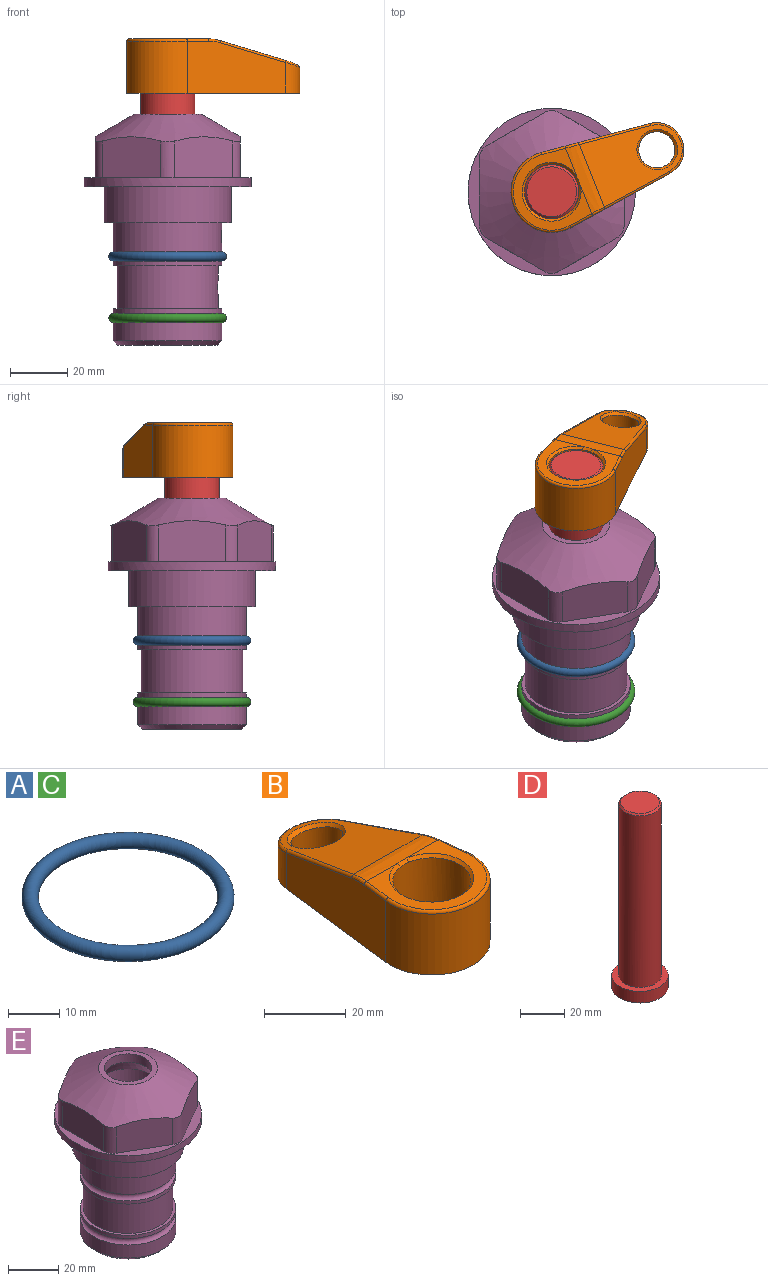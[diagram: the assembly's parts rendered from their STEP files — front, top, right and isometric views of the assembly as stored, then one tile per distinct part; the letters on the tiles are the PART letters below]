
ASSEMBLY  parts=5 mates=4
PART A: 1 faces, bbox 44.7x44.7x3.2 mm
  f0: torus R=19.05mm, axis (0,0,1), area 1193.9mm2
PART B: 31 faces, bbox 31.7x65.5x19.8 mm
  f0: plane 39.12x18.26mm, normal (0.99,0.12,0), area 612.2mm2, adj f1,f4,f7,f11,f13,f15
  f1: cylinder r=9.53mm len=18.91mm, axis (0,0,-1), area 296.1mm2, adj f0,f2,f7,f17
  f2: plane 39.12x18.26mm, normal (-0.99,0.12,0), area 612.2mm2, adj f1,f4,f7,f12,f14,f16
  f3: cylinder r=6.35mm len=12.7mm, axis (0,0,-1), area 362.4mm2, adj f7,f18
  f4: cylinder r=14.29mm len=28.58mm, axis (0,0,-1), area 882.2mm2, adj f0,f2,f7,f10
  f5: cylinder r=9.53mm len=19.05mm, axis (0,0,-1), area 1092.6mm2, adj f7,f19,f20
  f6: plane 26.99x23.69mm, normal (0,0,1), area 216.2mm2, adj f9,f10,f11,f12,f19
  f7: plane 63.5x28.58mm, normal (0,0,-1), area 661.8mm2, adj f0,f1,f2,f3,f4,f5,f22,f23
  f8: plane 33.52x23.6mm, normal (0,0.26,0.97), area 486mm2, adj f9,f15,f16,f17,f18
  f9: cylinder r=19.05mm len=24.72mm, axis (1,0,0), area 120.4mm2, adj f6,f8,f13,f14,f20
  f10: torus R=13.49mm, axis (0,0,1), area 59mm2, adj f4,f6,f11,f12
  f11: cylinder r=0.79mm len=8.67mm, axis (0.12,-0.99,0), area 10.8mm2, adj f0,f6,f10,f13
  f12: cylinder r=0.79mm len=8.67mm, axis (0.12,0.99,0), area 10.8mm2, adj f2,f6,f10,f14
  f13: bspline ~4.95x1.42mm, area 6.1mm2, adj f0,f9,f11,f15
  f14: bspline ~4.95x1.42mm, area 6.1mm2, adj f2,f9,f12,f16
  f15: cylinder r=0.79mm len=25.95mm, axis (0.12,-0.96,0.26), area 32.9mm2, adj f0,f8,f13,f17
  f16: cylinder r=0.79mm len=25.95mm, axis (0.12,0.96,-0.26), area 32.9mm2, adj f2,f8,f14,f17
  f17: bspline ~18.91x8.38mm, area 30mm2, adj f1,f8,f15,f16
  f18: bspline ~14.29x14.29mm, area 48.3mm2, adj f3,f8
  f19: cone r=9.53mm half-angle=45deg, axis (0,0,1), area 66.5mm2, adj f5,f6,f20
  f20: bspline ~3.22x0.96mm, area 3.5mm2, adj f5,f9,f19
  f21: plane 2.75x2.72mm, normal (0,0,-1), area 2.9mm2, adj f23,f25,f28
  f22: plane 23.05x15.88mm, normal (-0.99,-0.12,0), area 323.6mm2, adj f7,f25,f26,f27,f28,f29
  f23: plane 23.05x15.88mm, normal (0.99,-0.12,0), area 323.6mm2, adj f7,f21,f25,f27,f28,f30
  f24: cylinder r=9.53mm len=10.69mm, axis (0,0,-1), area 114.7mm2, adj f7,f27,f29,f30
  f25: cylinder r=12.7mm len=20.59mm, axis (0,0,-1), area 381.1mm2, adj f7,f21,f22,f23,f26,f28
  f26: plane 2.75x2.72mm, normal (0,0,-1), area 2.9mm2, adj f22,f25,f28
  f27: plane 19.72x18.37mm, normal (0,-0.26,-0.97), area 291.8mm2, adj f22,f23,f24,f28,f29,f30
  f28: cylinder r=15.88mm len=19.92mm, axis (1,0,0), area 54.8mm2, adj f21,f22,f23,f25,f26,f27
  f29: cylinder r=1.59mm len=11mm, axis (0,0,-1), area 34.7mm2, adj f7,f22,f24,f27
  f30: cylinder r=1.59mm len=11mm, axis (0,0,-1), area 34.7mm2, adj f7,f23,f24,f27
PART C: same geometry as A
PART D: 6 faces, bbox 25.4x25.4x101.6 mm
  f0: plane 17.46x17.46mm, normal (0,0,1), area 239.5mm2, adj f5
  f1: plane 25.4x25.4mm, normal (0,0,-1), area 506.7mm2, adj f2
  f2: cylinder r=12.7mm len=25.4mm, axis (0,0,1), area 506.7mm2, adj f1,f3
  f3: plane 25.4x25.4mm, normal (0,0,1), area 221.7mm2, adj f2,f4
  f4: cylinder r=9.53mm len=94.46mm, axis (0,0,1), area 5653mm2, adj f3,f5
  f5: cone r=8.73mm half-angle=45deg, axis (0,0,-1), area 64.4mm2, adj f0,f4
PART E: 36 faces, bbox 58.7x58.7x81 mm
  f0: cylinder r=17.78mm len=35.56mm, axis (0,0,1), area 1670.8mm2, adj f23,f24,f31
  f1: cylinder r=19.05mm len=38.1mm, axis (0,0,1), area 1191.9mm2, adj f26,f27,f30
  f2: plane 58.66x58.66mm, normal (0,0,-1), area 1150.6mm2, adj f3,f28
  f3: cylinder r=29.33mm len=58.66mm, axis (0,0,-1), area 585.1mm2, adj f2,f4
  f4: plane 58.66x58.66mm, normal (0,0,1), area 475.9mm2, adj f3,f5,f6,f7,f8,f9,f10,f11
  f5: plane 20.32x14.34mm, normal (-0.5,0.87,0), area 324.4mm2, adj f4,f15,f16,f17
  f6: plane 20.32x14.34mm, normal (0.5,0.87,0), area 324.4mm2, adj f4,f14,f15,f17
  f7: plane 23.48x14.34mm, normal (1,0,0), area 324.4mm2, adj f4,f13,f14,f17
  f8: plane 20.32x14.34mm, normal (0.5,-0.87,0), area 324.4mm2, adj f4,f12,f13,f17
  f9: plane 20.32x14.34mm, normal (-0.5,-0.87,0), area 324.4mm2, adj f4,f11,f12,f17
  f10: plane 23.48x14.34mm, normal (-1,0,0), area 324.4mm2, adj f4,f11,f16,f17
  f11: cylinder r=5.08mm len=12.85mm, axis (0,0,-1), area 67.2mm2, adj f4,f9,f10,f17
  f12: cylinder r=5.08mm len=12.85mm, axis (0,0,-1), area 67.2mm2, adj f4,f8,f9,f17
  f13: cylinder r=5.08mm len=12.85mm, axis (0,0,-1), area 67.2mm2, adj f4,f7,f8,f17
  f14: cylinder r=5.08mm len=12.85mm, axis (0,0,-1), area 67.2mm2, adj f4,f6,f7,f17
  f15: cylinder r=5.08mm len=12.85mm, axis (0,0,-1), area 67.2mm2, adj f4,f5,f6,f17
  f16: cylinder r=5.08mm len=12.85mm, axis (0,0,-1), area 67.2mm2, adj f4,f5,f10,f17
  f17: cone r=11.73mm half-angle=60deg, axis (0,0,-1), area 2071.8mm2, adj f5,f6,f7,f8,f9,f10,f11,f12
  f18: plane 23.46x23.46mm, normal (0,0,1), area 147.4mm2, adj f17,f35
  f19: plane 34.93x34.93mm, normal (0,0,-1), area 958mm2, adj f29
  f20: cylinder r=19.05mm len=38.1mm, axis (0,0,1), area 760.1mm2, adj f21,f29
  f21: torus R=19.05mm, axis (0,0,1), area 565.3mm2, adj f20,f22
  f22: cylinder r=19.05mm len=38.1mm, axis (0,0,1), area 190mm2, adj f21,f23
  f23: plane 38.1x38.1mm, normal (0,0,1), area 146.9mm2, adj f0,f22
  f24: plane 38.1x38.1mm, normal (0,0,-1), area 146.9mm2, adj f0,f25
  f25: cylinder r=19.05mm len=38.1mm, axis (0,0,1), area 190mm2, adj f24,f26
  f26: torus R=19.05mm, axis (0,0,1), area 565.3mm2, adj f1,f25
  f27: plane 44.45x44.45mm, normal (0,0,-1), area 411.7mm2, adj f1,f28
  f28: cylinder r=22.23mm len=44.45mm, axis (0,0,1), area 1773.5mm2, adj f2,f27
  f29: cone r=19.05mm half-angle=45deg, axis (0,0,1), area 257.5mm2, adj f19,f20
  f30: cylinder r=3.17mm len=6.75mm, axis (-1,0,0), area 128mm2, adj f1,f33
  f31: cylinder r=3.17mm len=6.35mm, axis (-1,0,0), area 102.5mm2, adj f0,f33
  f32: plane 25.4x25.4mm, normal (0,0,1), area 506.7mm2, adj f33
  f33: cylinder r=12.7mm len=66.42mm, axis (0,0,-1), area 5236.2mm2, adj f30,f31,f32,f34
  f34: cone r=9.53mm half-angle=30deg, axis (0,0,-1), area 443.4mm2, adj f33,f35
  f35: cylinder r=9.53mm len=19.05mm, axis (0,0,-1), area 240.9mm2, adj f18,f34
PLACE A at identity
PLACE B rot(axis=(0,0,-1),68.2deg) t=(0,0,-11.65)mm
PLACE C t=(0,0,-21.59)mm
PLACE D rot(axis=(0,0,-1),68.2deg) t=(0,0,-12.45)mm
PLACE E at identity fixed
MATE fastened D.f2 <-> B.f4  axis (0,0,1) through (0,0,51.05)mm
MATE fastened A.f0 <-> E.f0  axis (0,0,1) through (0,0,-24.51)mm
MATE cylindrical D.f2 <-> E.f0  axis (0,0,-1) through (0,0,-50.55)mm
MATE fastened C.f0 <-> E.f0  axis (0,0,1) through (0,0,-46.1)mm
